# Revit family: CENTUM Spannbügel
name_source: partatom
category: HLS-Bauteile
revit_build: Autodesk Revit 2017 (Build: 20190507_1515(x64)
units: mm (PartAtom-declared; Revit-internal decimal feet)

## family parameters
Arbeitsebenenbasiert = Ja
Beim Laden mit Abzugskörper schneiden = Nein
Bemaßung runder Anschluss = Durchmesser verwenden
Gemeinsam genutzt = Ja
Immer vertikal = Nein
Raumberechnungspunkt = Nein
Teiletyp = Normal

## types (2) — shared parameters
Fabrikat = MEFA
Firma = MEFA Befestigungs- und Montagesysteme GmbH
Klemmdicke = 25 mm
Material = Stahl
Mutter = Sechskantmutter : Sechskantmutter M12
Profil = CENTUM
S = 6 mm  [stored 0.019685 ft]
U-Scheibe = Unterlegscheibe : Unterlegscheibe 13x24x2.5
Vorgabe-Ansicht = 1219 mm
max. zul. Last Fx = 3.00 kN
max. zul. Last Fy = 3.00 kN
max. zul. Last Fz = 10.00 kN
zero-valued in all types: min. Randabstand

## per-type parameters (varying)
| type | Artikelnummer | B1 | EAN | Gewicht | Gewicht pro Bauteil | Kurztext1 | Kurztext2 | L | Profiltyp | Rundstahlbügel | Spannwinkel |
| CENTUM Spannbügel XL 80 | 1660801011 | 95 mm | 4250928458476 | 1.30 kg | 1.30 kg | Spannbügel M12 CENTUM XL 80 | Profilhöhe 80 mm Klemmdicke 25 mm | 120 mm  [stored 0.393701 ft] | XL 80 | CENTUM Rundstahl U-Bügel : CENTUM Rundtsahl U-Bügel  95-160 M12 | CENTUM Spannwinkel : CENTUM Spannwinkel XL 80 |
| CENTUM Spannbügel XL100/XL120 | 1661001011 | 115 mm  [stored 0.377297 ft] | 4250928458483 | 1.49 kg | 1.49 kg | Spannbügel M12 CENTUM XL 100 / 120 | Profilhöhe 100 / 120 mm Klemmdicke 25 mm | 140 mm  [stored 0.459318 ft] | XL 100, XL 120 | CENTUM Rundstahl U-Bügel : CENTUM Rundstahl U-Bügel 115-180 M12 | CENTUM Spannwinkel : CENTUM Spannwinkel XL100 |

note: [stored X ft] marks values corroborated as IEEE doubles in the binary element streams (Revit-internal decimal feet)

## geometry (parser evidence)
native form markers: Sweep x6
no freeform markers — native parametric forms only
